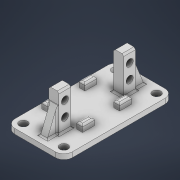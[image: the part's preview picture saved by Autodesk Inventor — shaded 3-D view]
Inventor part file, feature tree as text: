
AUTODESK INVENTOR PART (.ipt)
format: ipt  version: 2021 (Build 250183000, 183)  size: 261,120 bytes
history: native  units: mm
features: sketch x5, extrude x3, hole x2, plane x2, fillet x2, rib x1, chamfer x1, mirror x1
ambient origin geometry x8: Origin, YZ Plane, XZ Plane, XY Plane, X Axis, Y Axis, Z Axis, Center Point
bodies: Solid1 (feature_tree)
feature tree (17):
  extrude  "Extrusion1"  Depth=65.0mm
  sketch  "Sketch2"  dims[d2=3.0mm d3=0.0mm d5=5.8mm]
  extrude  "Extrusion2"  Depth=5.8mm
  hole  "Hole1"  [1 undecoded]
  extrude  "Extrusion3"  Depth=6.0mm
  plane  "Work Plane1"
  rib  "Rib1"
  fillet  "Fillet1"  Radius=22.0mm
  chamfer  "Chamfer1"  Distance=6.0mm
  plane  "Work Plane2"
  mirror  "Mirror2"
  fillet  "Fillet4"  Radius=7.0mm
  hole  "Hole4"  [1 undecoded]
  sketch  "Sketch1"  dims[d0=34.0mm d1=65.0mm]
  sketch  "Sketch3"  dims[d6=7.4mm d7=2.3mm]
  sketch  "Sketch4"  dims[d8=28.0mm d11=6.0mm d12=22.0mm d13=0.0mm]
  sketch  "Sketch7"  dims[d14=8.6mm d15=6.0mm d16=4.2mm d17=6.0mm d18=4.0mm d19=2.0mm d20=90.0deg d21=0.8mm d22=0.0mm d23=7.0mm d24=7.0mm d25=3.5mm d26=7.0mm d27=3.5mm d28=3.75mm d29=0.0mm d30=7.0mm d31=15.0mm d32=6.0mm d33=1.0mm d34=4.0mm d35=0.0mm d36=0.0mm d37=1.0mm d38=1.0mm d39=1.0mm d40=1.0mm d41=2.0mm d42=45.0deg d59=5.0mm d60=4.9mm d61=6.0mm d62=4.0mm d63=2.0mm d64=90.0deg d65=0.8mm d66=0.0mm d67=19.2mm d44=1.0mm d45=1.0mm d46=1.0mm d47=0.15mm d48=0.25mm d49=0.375mm d50=14.3117mm d51=0.75mm d52=20.594885mm d53=0.0625mm d54=0.75mm d55=0.375mm]
note: 2 required parameter values undecoded (feature->parameter linkage not recoverable at this tier; creation-order binding heuristic only, values carry confidence <= 0.55)
